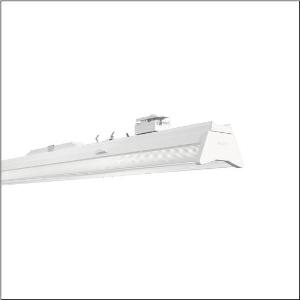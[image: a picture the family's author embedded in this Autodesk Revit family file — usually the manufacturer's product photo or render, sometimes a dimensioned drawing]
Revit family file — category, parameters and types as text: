
# Revit family: licross_r__21_performance_mo_52td16vn465g_2158
name_source: partatom
category: Lighting Fixtures
units: mm (PartAtom-declared; Revit-internal decimal feet)

## family parameters
Cut with Voids When Loaded = No
Host = Face
Light Source = No
Part Type = Normal
Room Calculation Point = No
Round Connector Dimension = Use Diameter
Shared = No

## types (1)
- --- (1 x LED, 6500 lm, 36.1 W, 4000K)
    Apparent Load = 36 VA
    CIE Flux Codes = 66 88 96 79 100
    Color Rendering = 80
    Color Temperature = 4000K
    Default Elevation = 1800 mm
    Description = Licross® 21 Performance MO, luminaire insert, of sheet steel, galvanised, coil coated, white, length: 1.500mm, width: 120mm, height: 123mm, LED rated luminous flux: 6.500lm, light colour: 840, control gear: DALI 2, CLO, with plug, 5-pole, with phase selection, mains connection: 220..240V, AC, 50/60Hz, start of lifetime: 36W, end of service life: 43W, halogen-free wiring, primary light control with lens, of plastic, primary optical cover: cover, of PMMA, light emission: direct/indirect distribution, primary light characteristic: symmetric, protection rating (complete): IP54, insulation class (complete): insulation class I (protective earthing), certification: CE, ENEC, VDE, UKCA, protection symbol: D if used in an environment with non-conductive dust loads with corresponding accessories, impact resistance: IK06, permissible ambient temperature for indoor applications: -25..+45°C, corresponds to IFS (International Featured Standards) requirements for safety and quality in the food industry, reducing of maximum allowable ambient temperature of 5°C with ceiling mounting, LABS conformity tested according to VDMA 24364:2018-05, packaging unit: 1 piece
    Height = 114 mm
    Lamp = 1 x LED
    Lamp Light Flux = 6500 lm
    Lamp Power = 36.1 W
    Lamp count = 1
    Length = 1500 mm
    Luminous efficacy = 180 lm/W
    Manufacturer = Siteco
    ModVariant = No
    Model = 52TD16VN465G
    Mounting Place = Ceiling
    Mounting Type = Pendant
    Number of Poles = 1
    OnlyDefault = Yes
    Power Factor = 1
    Product Name = Licross® 21 Performance MO
    Product group = luminaire insert
    ProductGroupID = 901
    Protection Class = Protection class I
    Protection Degree = IP 54
    RLX_Detail_Level = 1
    RLX_Emergency_Light_Flux = 0 lm
    RLX_Emergency_Type = 0
    RLX_Emergency_Type_DB = No
    RlxData = <blob elided: 34073 chars, md5=d90805e4>
    Socket = socket
    Standby Power = 0 W
    System Light Flux = 6500 lm
    System Power = 36 W
    Type Comments = factory setting: luminous flux: 100 % | dim-lin: 254 | 242 mA
    Type Image = l_1256138.jpg
    URL = http://relux.com
    VarID = @adj_035377
    Voltage = 0 V
    Weight = 0.00 kg
    Width = 120 mm

## geometry (parser evidence)
native form markers: Blend x4, Sweep x13
no freeform markers — native parametric forms only
